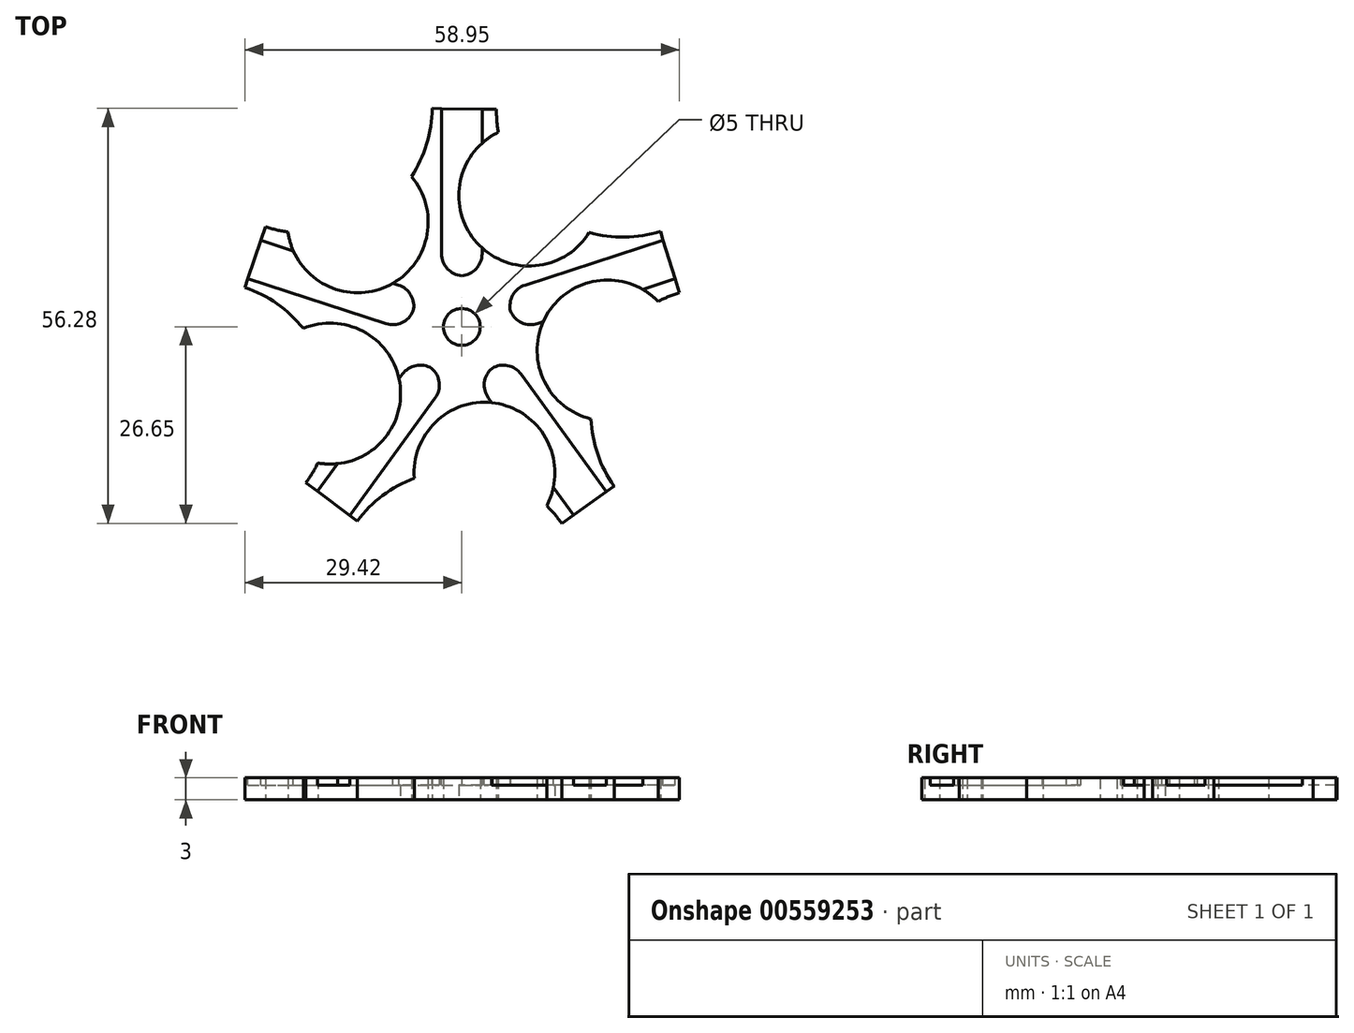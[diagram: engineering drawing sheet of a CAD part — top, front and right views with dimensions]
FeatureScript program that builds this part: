
annotation { "Feature Type Name" : "Feature", "Feature Type Description" : "" }
export const myFeature = defineFeature(function(context is Context, id is Id, definition is map)
    precondition{}
    {
        {
            var Q0;
            Q0=qCreatedBy(makeId("Top.planeOp"),FACE);
            var sketch = newSketch(context, id + "F0", { "sketchPlane" : qUnion([Q0])});
            skLineSegment(sketch, "E0.bottom", {"start": v(0, 0) * mm, "end": v(75, 0) * mm, "construction": true});
            skLineSegment(sketch, "E0.top", {"start": v(0, 75) * mm, "end": v(75, 75) * mm, "construction": true});
            skLineSegment(sketch, "E0.left", {"start": v(0, 0) * mm, "end": v(0, 75) * mm, "construction": true});
            skLineSegment(sketch, "E0.right", {"start": v(75, 0) * mm, "end": v(75, 75) * mm, "construction": true});
            skCircle(sketch, "E1", {"center": v(37.5, 37.5) * mm, "radius": 2.5 * mm});
            skCircle(sketch, "E2.cCircle", {"center": v(37.5, 37.5) * mm, "radius": 29.58 * mm, "construction": true});
            skLineSegment(sketch, "E2.0", {"start": v(33.5, 67.13) * mm, "end": v(42.2, 67.03) * mm});
            skLineSegment(sketch, "E2.1", {"start": v(64.44, 50.47) * mm, "end": v(67.03, 42.16) * mm});
            skLineSegment(sketch, "E2.2", {"start": v(58.16, 15.88) * mm, "end": v(51.05, 10.85) * mm});
            skLineSegment(sketch, "E2.3", {"start": v(23.33, 11.17) * mm, "end": v(16.34, 16.37) * mm});
            skLineSegment(sketch, "E2.4", {"start": v(8.08, 42.84) * mm, "end": v(10.87, 51.1) * mm});
            skPoint(sketch, "E2.0.midPoint", {"position": v(37.85, 67.08) * mm});
            skArc(sketch, "E3", {"start": v(10.87, 51.1) * mm, "mid": v(12.38, 50.66) * mm, "end": v(13.92, 50.37) * mm});
            skArc(sketch, "E4.1.0", {"start": v(16.34, 16.37) * mm, "mid": v(17.22, 17.67) * mm, "end": v(17.97, 19.05) * mm});
            skArc(sketch, "E4.2.0", {"start": v(51.05, 10.85) * mm, "mid": v(50.1, 12.09) * mm, "end": v(49.02, 13.23) * mm});
            skArc(sketch, "E4.3.0", {"start": v(67.03, 42.16) * mm, "mid": v(65.56, 41.62) * mm, "end": v(64.14, 40.95) * mm});
            skArc(sketch, "E4.4.0", {"start": v(42.2, 67.03) * mm, "mid": v(42.25, 65.46) * mm, "end": v(42.45, 63.9) * mm});
            skArc(sketch, "E5", {"start": v(13.92, 50.37) * mm, "mid": v(27.3, 42.98) * mm, "end": v(30.66, 57.89) * mm});
            skArc(sketch, "E6.1.0", {"start": v(17.97, 19.05) * mm, "mid": v(29.13, 29.49) * mm, "end": v(16, 37.3) * mm});
            skArc(sketch, "E6.2.0", {"start": v(49.02, 13.23) * mm, "mid": v(42.54, 27.07) * mm, "end": v(31.05, 16.98) * mm});
            skArc(sketch, "E6.3.0", {"start": v(64.14, 40.95) * mm, "mid": v(48.98, 39.07) * mm, "end": v(55.02, 25.03) * mm});
            skArc(sketch, "E6.4.0", {"start": v(42.45, 63.9) * mm, "mid": v(39.56, 48.9) * mm, "end": v(54.78, 50.3) * mm});
            skArc(sketch, "E7.trimOffspring", {"start": v(30.66, 57.89) * mm, "mid": v(32.74, 62.3) * mm, "end": v(33.5, 67.13) * mm});
            skArc(sketch, "E8.trimOffspring", {"start": v(54.78, 50.3) * mm, "mid": v(59.62, 49.7) * mm, "end": v(64.44, 50.47) * mm});
            skArc(sketch, "E9.trimOffspring", {"start": v(55.02, 25.03) * mm, "mid": v(55.93, 20.23) * mm, "end": v(58.16, 15.88) * mm});
            skArc(sketch, "E10.trimOffspring", {"start": v(31.05, 16.98) * mm, "mid": v(26.77, 14.64) * mm, "end": v(23.33, 11.17) * mm});
            skArc(sketch, "E11.trimOffspring", {"start": v(16, 37.3) * mm, "mid": v(12.44, 40.64) * mm, "end": v(8.08, 42.84) * mm});
            skSolve(sketch);
        }
        {
            var Q0;
            Q0=makeQuery(id+"F0.imprint","IMPRINT",FACE,{"disambiguationData":[TD([[makeQuery(id+"F0.imprint","IMPRINT",EDGE,{"derivedFrom":sQuery(id+"F0.wireOp",EDGE,"E1")}),-1.0]])]});
            extrude(context, id + "F1", {"entities" : qUnion([Q0]), "depth" : 3 * mm, "offsetDistance" : 25 * mm});
        }
        {
            var Q0;
            Q0=makeQuery(id+"F1.opExtrude","CAP_FACE",FACE,{"disambiguationData":[OSD([sQuery(id+"F0.wireOp",EDGE,"E1"),sQuery(id+"F0.wireOp",EDGE,"E2.0"),sQuery(id+"F0.wireOp",EDGE,"E2.1"),sQuery(id+"F0.wireOp",EDGE,"E2.2"),sQuery(id+"F0.wireOp",EDGE,"E2.3"),sQuery(id+"F0.wireOp",EDGE,"E2.4"),sQuery(id+"F0.wireOp",EDGE,"E3"),sQuery(id+"F0.wireOp",EDGE,"E4.1.0"),sQuery(id+"F0.wireOp",EDGE,"E4.2.0"),sQuery(id+"F0.wireOp",EDGE,"E4.3.0"),sQuery(id+"F0.wireOp",EDGE,"E4.4.0"),sQuery(id+"F0.wireOp",EDGE,"E5"),sQuery(id+"F0.wireOp",EDGE,"E6.1.0"),sQuery(id+"F0.wireOp",EDGE,"E6.2.0"),sQuery(id+"F0.wireOp",EDGE,"E6.3.0"),sQuery(id+"F0.wireOp",EDGE,"E6.4.0"),sQuery(id+"F0.wireOp",EDGE,"E7.trimOffspring"),sQuery(id+"F0.wireOp",EDGE,"E8.trimOffspring"),sQuery(id+"F0.wireOp",EDGE,"E9.trimOffspring"),sQuery(id+"F0.wireOp",EDGE,"E10.trimOffspring"),sQuery(id+"F0.wireOp",EDGE,"E11.trimOffspring")])],"isStart":false});
            var sketch = newSketch(context, id + "F2", { "sketchPlane" : qUnion([Q0])});
            skCircle(sketch, "E12.0", {"center": v(37.5, 37.5) * mm, "radius": 2.5 * mm});
            skLineSegment(sketch, "E13.0", {"start": v(33.5, 67.13) * mm, "end": v(42.2, 67.03) * mm});
            skLineSegment(sketch, "E14.bottom", {"start": v(34.75, 67.11) * mm, "end": v(40.25, 67.11) * mm});
            skLineSegment(sketch, "E14.top", {"start": v(34.75, 44.43) * mm, "end": v(40.25, 44.43) * mm});
            skLineSegment(sketch, "E14.left", {"start": v(34.75, 67.11) * mm, "end": v(34.75, 44.43) * mm});
            skLineSegment(sketch, "E14.right", {"start": v(40.25, 67.11) * mm, "end": v(40.25, 44.43) * mm});
            skLineSegment(sketch, "E15", {"start": v(37.5, 37.5) * mm, "end": v(37.5, 44.43) * mm});
            skLineSegment(sketch, "E16.1.0", {"start": v(10.18, 49.27) * mm, "end": v(31.76, 42.26) * mm});
            skLineSegment(sketch, "E16.1.1", {"start": v(8.48, 44.04) * mm, "end": v(10.18, 49.27) * mm});
            skLineSegment(sketch, "E16.1.2", {"start": v(8.48, 44.04) * mm, "end": v(30.06, 37.03) * mm});
            skLineSegment(sketch, "E16.1.3", {"start": v(30.06, 37.03) * mm, "end": v(31.76, 42.26) * mm});
            skLineSegment(sketch, "E16.2.0", {"start": v(17.87, 15.16) * mm, "end": v(31.2, 33.5) * mm});
            skLineSegment(sketch, "E16.2.1", {"start": v(22.32, 11.92) * mm, "end": v(17.87, 15.16) * mm});
            skLineSegment(sketch, "E16.2.2", {"start": v(22.32, 11.92) * mm, "end": v(35.65, 30.28) * mm});
            skLineSegment(sketch, "E16.2.3", {"start": v(35.65, 30.28) * mm, "end": v(31.2, 33.5) * mm});
            skLineSegment(sketch, "E16.3.0", {"start": v(52.68, 11.92) * mm, "end": v(39.35, 30.28) * mm});
            skLineSegment(sketch, "E16.3.1", {"start": v(57.13, 15.16) * mm, "end": v(52.68, 11.92) * mm});
            skLineSegment(sketch, "E16.3.2", {"start": v(57.13, 15.16) * mm, "end": v(43.8, 33.5) * mm});
            skLineSegment(sketch, "E16.3.3", {"start": v(43.8, 33.5) * mm, "end": v(39.35, 30.28) * mm});
            skLineSegment(sketch, "E16.4.0", {"start": v(66.52, 44.04) * mm, "end": v(44.94, 37.03) * mm});
            skLineSegment(sketch, "E16.4.1", {"start": v(64.82, 49.27) * mm, "end": v(66.52, 44.04) * mm});
            skLineSegment(sketch, "E16.4.2", {"start": v(64.82, 49.27) * mm, "end": v(43.24, 42.26) * mm});
            skLineSegment(sketch, "E16.4.3", {"start": v(43.24, 42.26) * mm, "end": v(44.94, 37.03) * mm});
            skSolve(sketch);
        }
        {
            var Q0;
            Q0=makeQuery(id+"F2.imprint","IMPRINT",FACE,{"disambiguationData":[TD([[makeQuery(id+"F2.imprint","IMPRINT",EDGE,{"derivedFrom":sQuery(id+"F2.wireOp",EDGE,"E14.bottom")}),-1.0]])]});
            var Q1;
            Q1=makeQuery(id+"F2.imprint","IMPRINT",FACE,{"disambiguationData":[TD([[makeQuery(id+"F2.imprint","IMPRINT",EDGE,{"derivedFrom":sQuery(id+"F2.wireOp",EDGE,"E16.1.0")}),-1.0]])]});
            var Q2;
            Q2=makeQuery(id+"F2.imprint","IMPRINT",FACE,{"disambiguationData":[TD([[makeQuery(id+"F2.imprint","IMPRINT",EDGE,{"derivedFrom":sQuery(id+"F2.wireOp",EDGE,"E16.2.0")}),-1.0]])]});
            var Q3;
            Q3=makeQuery(id+"F2.imprint","IMPRINT",FACE,{"disambiguationData":[TD([[makeQuery(id+"F2.imprint","IMPRINT",EDGE,{"derivedFrom":sQuery(id+"F2.wireOp",EDGE,"E16.3.0")}),-1.0]])]});
            var Q4;
            Q4=makeQuery(id+"F2.imprint","IMPRINT",FACE,{"disambiguationData":[TD([[makeQuery(id+"F2.imprint","IMPRINT",EDGE,{"derivedFrom":sQuery(id+"F2.wireOp",EDGE,"E16.4.0")}),-1.0]])]});
            var Q5;
            {var subQ4=sQuery(id+"F2.wireOp",EDGE,"E14.left");Q5=makeQuery(id+"F2.imprint","IMPRINT",FACE,{"disambiguationData":[TD([[makeQuery(id+"F2.imprint","IMPRINT",EDGE,{"derivedFrom":subQ4}),1.0]])]});}
            extrude(context, id + "F3", {"entities" : qUnion([Q0, Q1, Q2, Q3, Q4, Q5]), "operationType" : NewBodyOperationType.REMOVE, "oppositeDirection" : true, "depth" : 1 * mm, "offsetDistance" : 25 * mm});
        }
        {
            var Q0;
            Q0=makeQuery(id+"F3.boolean.opBoolean","COPY",EDGE,{"derivedFrom":makeQuery(id+"F3.opExtrude","SWEPT_EDGE",EDGE,{"disambiguationData":[OSD([sQuery(id+"F2.wireOp",EDGE,"E14.top"),sQuery(id+"F2.wireOp",EDGE,"E14.right")])]})});
            var Q1;
            Q1=makeQuery(id+"F3.boolean.opBoolean","COPY",EDGE,{"derivedFrom":makeQuery(id+"F3.opExtrude","SWEPT_EDGE",EDGE,{"disambiguationData":[OSD([sQuery(id+"F2.wireOp",EDGE,"E14.top"),sQuery(id+"F2.wireOp",EDGE,"E14.left")])]})});
            var Q2;
            Q2=makeQuery(id+"F3.boolean.opBoolean","COPY",EDGE,{"derivedFrom":makeQuery(id+"F3.opExtrude","SWEPT_EDGE",EDGE,{"disambiguationData":[OSD([sQuery(id+"F2.wireOp",EDGE,"E16.1.0"),sQuery(id+"F2.wireOp",EDGE,"E16.1.3")])]})});
            var Q3;
            Q3=makeQuery(id+"F3.boolean.opBoolean","COPY",EDGE,{"derivedFrom":makeQuery(id+"F3.opExtrude","SWEPT_EDGE",EDGE,{"disambiguationData":[OSD([sQuery(id+"F2.wireOp",EDGE,"E16.1.2"),sQuery(id+"F2.wireOp",EDGE,"E16.1.3")])]})});
            var Q4;
            Q4=makeQuery(id+"F3.boolean.opBoolean","COPY",EDGE,{"derivedFrom":makeQuery(id+"F3.opExtrude","SWEPT_EDGE",EDGE,{"disambiguationData":[OSD([sQuery(id+"F2.wireOp",EDGE,"E16.2.0"),sQuery(id+"F2.wireOp",EDGE,"E16.2.3")])]})});
            var Q5;
            Q5=makeQuery(id+"F3.boolean.opBoolean","COPY",EDGE,{"derivedFrom":makeQuery(id+"F3.opExtrude","SWEPT_EDGE",EDGE,{"disambiguationData":[OSD([sQuery(id+"F2.wireOp",EDGE,"E16.2.2"),sQuery(id+"F2.wireOp",EDGE,"E16.2.3")])]})});
            var Q6;
            Q6=makeQuery(id+"F3.boolean.opBoolean","COPY",EDGE,{"derivedFrom":makeQuery(id+"F3.opExtrude","SWEPT_EDGE",EDGE,{"disambiguationData":[OSD([sQuery(id+"F2.wireOp",EDGE,"E16.3.0"),sQuery(id+"F2.wireOp",EDGE,"E16.3.3")])]})});
            var Q7;
            Q7=makeQuery(id+"F3.boolean.opBoolean","COPY",EDGE,{"derivedFrom":makeQuery(id+"F3.opExtrude","SWEPT_EDGE",EDGE,{"disambiguationData":[OSD([sQuery(id+"F2.wireOp",EDGE,"E16.3.2"),sQuery(id+"F2.wireOp",EDGE,"E16.3.3")])]})});
            var Q8;
            Q8=makeQuery(id+"F3.boolean.opBoolean","COPY",EDGE,{"derivedFrom":makeQuery(id+"F3.opExtrude","SWEPT_EDGE",EDGE,{"disambiguationData":[OSD([sQuery(id+"F2.wireOp",EDGE,"E16.4.0"),sQuery(id+"F2.wireOp",EDGE,"E16.4.3")])]})});
            var Q9;
            Q9=makeQuery(id+"F3.boolean.opBoolean","COPY",EDGE,{"derivedFrom":makeQuery(id+"F3.opExtrude","SWEPT_EDGE",EDGE,{"disambiguationData":[OSD([sQuery(id+"F2.wireOp",EDGE,"E16.4.2"),sQuery(id+"F2.wireOp",EDGE,"E16.4.3")])]})});
            fillet(context, id + "F4", {"entities" : qUnion([Q0, Q1, Q2, Q3, Q4, Q5, Q6, Q7, Q8, Q9]), "radius" : 3 * mm, "tangentPropagation" : true, "allowEdgeOverflow" : false});
        }
    });
